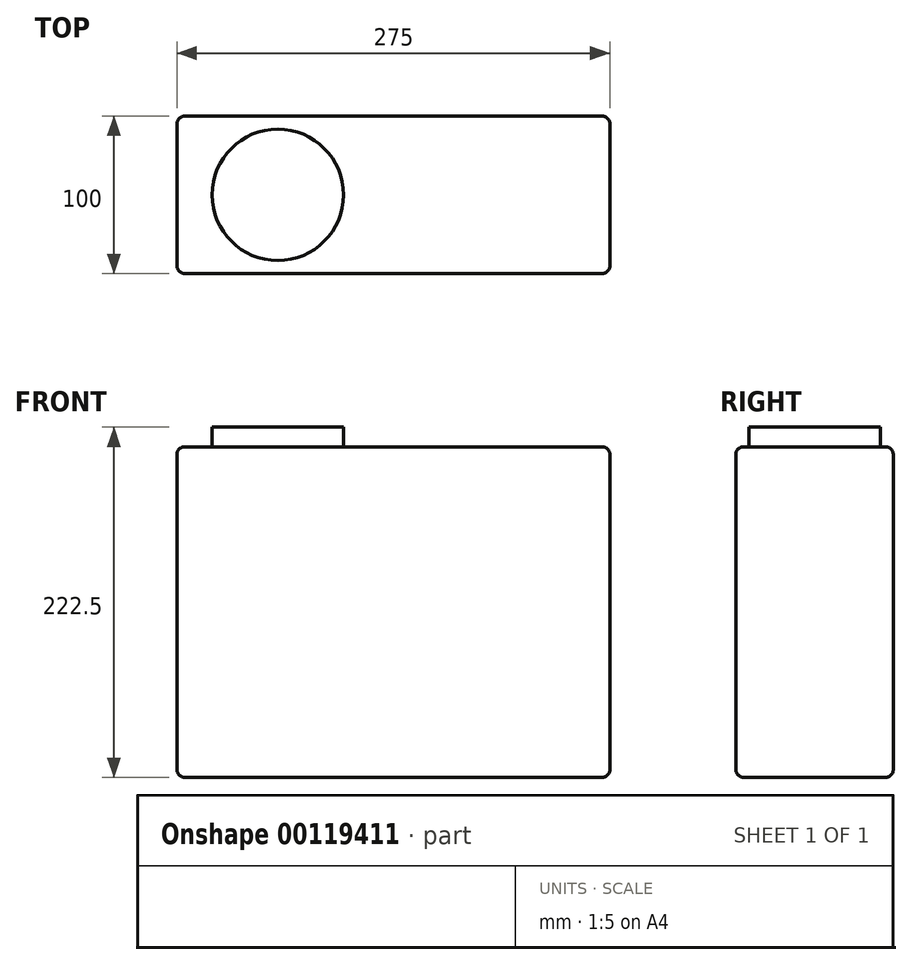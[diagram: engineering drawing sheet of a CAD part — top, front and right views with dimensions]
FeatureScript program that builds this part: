
annotation { "Feature Type Name" : "Feature", "Feature Type Description" : "" }
export const myFeature = defineFeature(function(context is Context, id is Id, definition is map)
    precondition{}
    {
        {
            var Q0;
            Q0=qCreatedBy(makeId("Front.planeOp"),FACE);
            var sketch = newSketch(context, id + "F0", { "sketchPlane" : qUnion([Q0])});
            skLineSegment(sketch, "E0.bottom", {"start": v(137.5, -105) * mm, "end": v(-137.5, -105) * mm});
            skLineSegment(sketch, "E0.top", {"start": v(137.5, 105) * mm, "end": v(-137.5, 105) * mm});
            skLineSegment(sketch, "E0.left", {"start": v(137.5, -105) * mm, "end": v(137.5, 105) * mm});
            skLineSegment(sketch, "E0.right", {"start": v(-137.5, -105) * mm, "end": v(-137.5, 105) * mm});
            skPoint(sketch, "E0.middle", {"position": v(0, 0) * mm});
            skSolve(sketch);
        }
        {
            var Q0;
            Q0=makeQuery(id+"F0.imprint","IMPRINT",FACE,{"disambiguationData":[TD([[makeQuery(id+"F0.imprint","IMPRINT",EDGE,{"derivedFrom":sQuery(id+"F0.wireOp",EDGE,"E0.bottom")}),-1.0]])]});
            extrude(context, id + "F1", {"entities" : qUnion([Q0]), "depth" : 100 * mm});
        }
        {
            var Q0;
            Q0=makeQuery(id+"F1.opExtrude","SWEPT_FACE",FACE,{"disambiguationData":[OSD([sQuery(id+"F0.wireOp",EDGE,"E0.right")])]});
            var Q1;
            Q1=makeQuery(id+"F1.opExtrude","SWEPT_FACE",FACE,{"disambiguationData":[OSD([sQuery(id+"F0.wireOp",EDGE,"E0.top")])]});
            var Q2;
            Q2=makeQuery(id+"F1.opExtrude","CAP_FACE",FACE,{"disambiguationData":[OSD([sQuery(id+"F0.wireOp",EDGE,"E0.bottom"),sQuery(id+"F0.wireOp",EDGE,"E0.top"),sQuery(id+"F0.wireOp",EDGE,"E0.left"),sQuery(id+"F0.wireOp",EDGE,"E0.right")])],"isStart":true});
            var Q3;
            Q3=makeQuery(id+"F1.opExtrude","SWEPT_FACE",FACE,{"disambiguationData":[OSD([sQuery(id+"F0.wireOp",EDGE,"E0.left")])]});
            var Q4;
            Q4=makeQuery(id+"F1.opExtrude","SWEPT_FACE",FACE,{"disambiguationData":[OSD([sQuery(id+"F0.wireOp",EDGE,"E0.bottom")])]});
            fillet(context, id + "F2", {"entities" : qUnion([Q0, Q1, Q2, Q3, Q4]), "radius" : 5 * mm, "tangentPropagation" : true, "allowEdgeOverflow" : false});
        }
        {
            var Q0;
            Q0=makeQuery(id+"F1.opExtrude","SWEPT_FACE",FACE,{"disambiguationData":[OSD([sQuery(id+"F0.wireOp",EDGE,"E0.top")])]});
            var sketch = newSketch(context, id + "F3", { "sketchPlane" : qUnion([Q0])});
            skCircle(sketch, "E1", {"center": v(-73.4, -50) * mm, "radius": 41.71 * mm});
            skPoint(sketch, "E1.centerSnap0", {"position": v(-132.5, -50) * mm});
            skSolve(sketch);
        }
        {
            var Q0;
            Q0=makeQuery(id+"F3.imprint","IMPRINT",FACE,{"disambiguationData":[TD([[makeQuery(id+"F3.imprint","IMPRINT",EDGE,{"derivedFrom":sQuery(id+"F3.wireOp",EDGE,"E1")}),1.0]])]});
            extrude(context, id + "F4", {"entities" : qUnion([Q0]), "operationType" : NewBodyOperationType.ADD, "depth" : 12.5 * mm});
        }
    });
